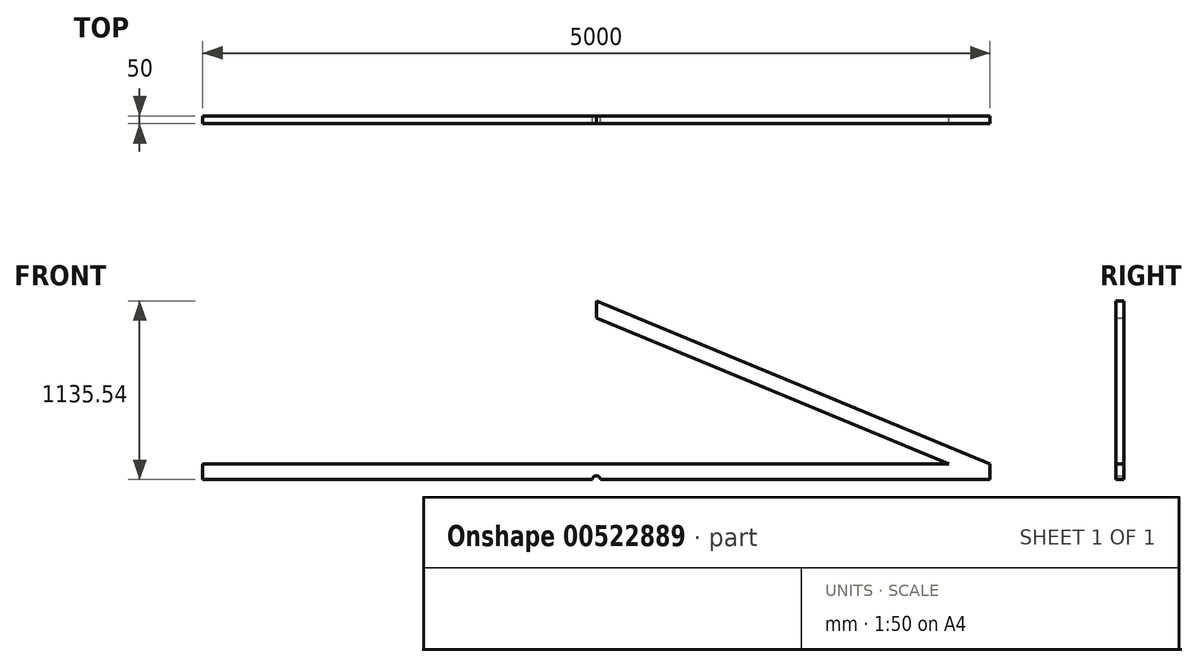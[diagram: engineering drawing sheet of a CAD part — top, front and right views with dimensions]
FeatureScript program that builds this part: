
annotation { "Feature Type Name" : "Feature", "Feature Type Description" : "" }
export const myFeature = defineFeature(function(context is Context, id is Id, definition is map)
    precondition{}
    {
        {
            var Q0;
            Q0=qCreatedBy(makeId("Front.planeOp"),FACE);
            var sketch = newSketch(context, id + "F0", { "sketchPlane" : qUnion([Q0])});
            skLineSegment(sketch, "E0", {"start": v(-701.21, 56.77) * mm, "end": v(4298.79, 56.77) * mm});
            skLineSegment(sketch, "E1", {"start": v(4298.79, 56.77) * mm, "end": v(4298.79, -43.23) * mm});
            skLineSegment(sketch, "E2", {"start": v(4298.79, -43.23) * mm, "end": v(1823.79, -43.23) * mm});
            skLineSegment(sketch, "E3", {"start": v(-701.21, -43.23) * mm, "end": v(-701.21, 56.77) * mm});
            skLineSegment(sketch, "E4", {"start": v(1798.79, 56.77) * mm, "end": v(1748.79, 56.77) * mm});
            skLineSegment(sketch, "E5", {"start": v(1848.79, 56.77) * mm, "end": v(1798.79, 56.77) * mm});
            skLineSegment(sketch, "E6", {"start": v(4298.79, 56.77) * mm, "end": v(1798.79, 1092.3) * mm});
            skLineSegment(sketch, "E7", {"start": v(1798.79, 1092.3) * mm, "end": v(1798.79, 984.07) * mm});
            skLineSegment(sketch, "E8", {"start": v(1798.79, 984.07) * mm, "end": v(4037.48, 56.77) * mm});
            skLineSegment(sketch, "E9", {"start": v(4037.48, 56.77) * mm, "end": v(4298.79, 56.77) * mm});
            skLineSegment(sketch, "E10", {"start": v(1798.79, 984.07) * mm, "end": v(-439.9, 56.77) * mm});
            skLineSegment(sketch, "E11", {"start": v(-439.9, 56.77) * mm, "end": v(-701.21, 56.77) * mm});
            skLineSegment(sketch, "E12", {"start": v(1798.79, 984.07) * mm, "end": v(1798.79, 1092.3) * mm});
            skLineSegment(sketch, "E13", {"start": v(1798.79, 1092.3) * mm, "end": v(-701.21, 56.77) * mm});
            skLineSegment(sketch, "E14", {"start": v(1848.79, 963.36) * mm, "end": v(1798.79, 984.07) * mm});
            skLineSegment(sketch, "E15", {"start": v(1848.79, 56.77) * mm, "end": v(1848.79, 963.36) * mm});
            skLineSegment(sketch, "E16", {"start": v(1748.79, 963.36) * mm, "end": v(1748.79, 56.77) * mm});
            skArc(sketch, "E17", {"start": v(1823.79, -43.23) * mm, "mid": v(1798.79, -18.23) * mm, "end": v(1773.79, -43.23) * mm});
            skLineSegment(sketch, "E18.trimOffspring", {"start": v(1773.79, -43.23) * mm, "end": v(-701.21, -43.23) * mm});
            skPoint(sketch, "E19", {"position": v(-601.21, -43.23) * mm});
            skPoint(sketch, "E20", {"position": v(4198.79, -43.23) * mm});
            skSolve(sketch);
        }
        {
            var Q0;
            {var subQ1=sQuery(id+"F0.wireOp",EDGE,"E11");Q0=makeQuery(id+"F0.imprint","IMPRINT",FACE,{"disambiguationData":[TD([[makeQuery(id+"F0.imprint","IMPRINT",EDGE,{"derivedFrom":subQ1}),-1.0]])]});}
            var Q1;
            Q1=makeQuery(id+"F0.imprint","IMPRINT",FACE,{"disambiguationData":[TD([[makeQuery(id+"F0.imprint","IMPRINT",EDGE,{"derivedFrom":sQuery(id+"F0.wireOp",EDGE,"E4")}),-1.0]])]});
            var Q2;
            Q2=makeQuery(id+"F0.imprint","IMPRINT",FACE,{"disambiguationData":[TD([[makeQuery(id+"F0.imprint","IMPRINT",EDGE,{"derivedFrom":sQuery(id+"F0.wireOp",EDGE,"E6")}),1.0]])]});
            var Q3;
            Q3=makeQuery(id+"F0.imprint","IMPRINT",FACE,{"disambiguationData":[TD([[makeQuery(id+"F0.imprint","IMPRINT",EDGE,{"derivedFrom":sQuery(id+"F0.wireOp",EDGE,"E1")}),-1.0]])]});
            extrude(context, id + "F1", {"entities" : qUnion([Q0, Q1, Q2, Q3]), "depth" : 50 * mm, "offsetDistance" : 25 * mm});
        }
    });
